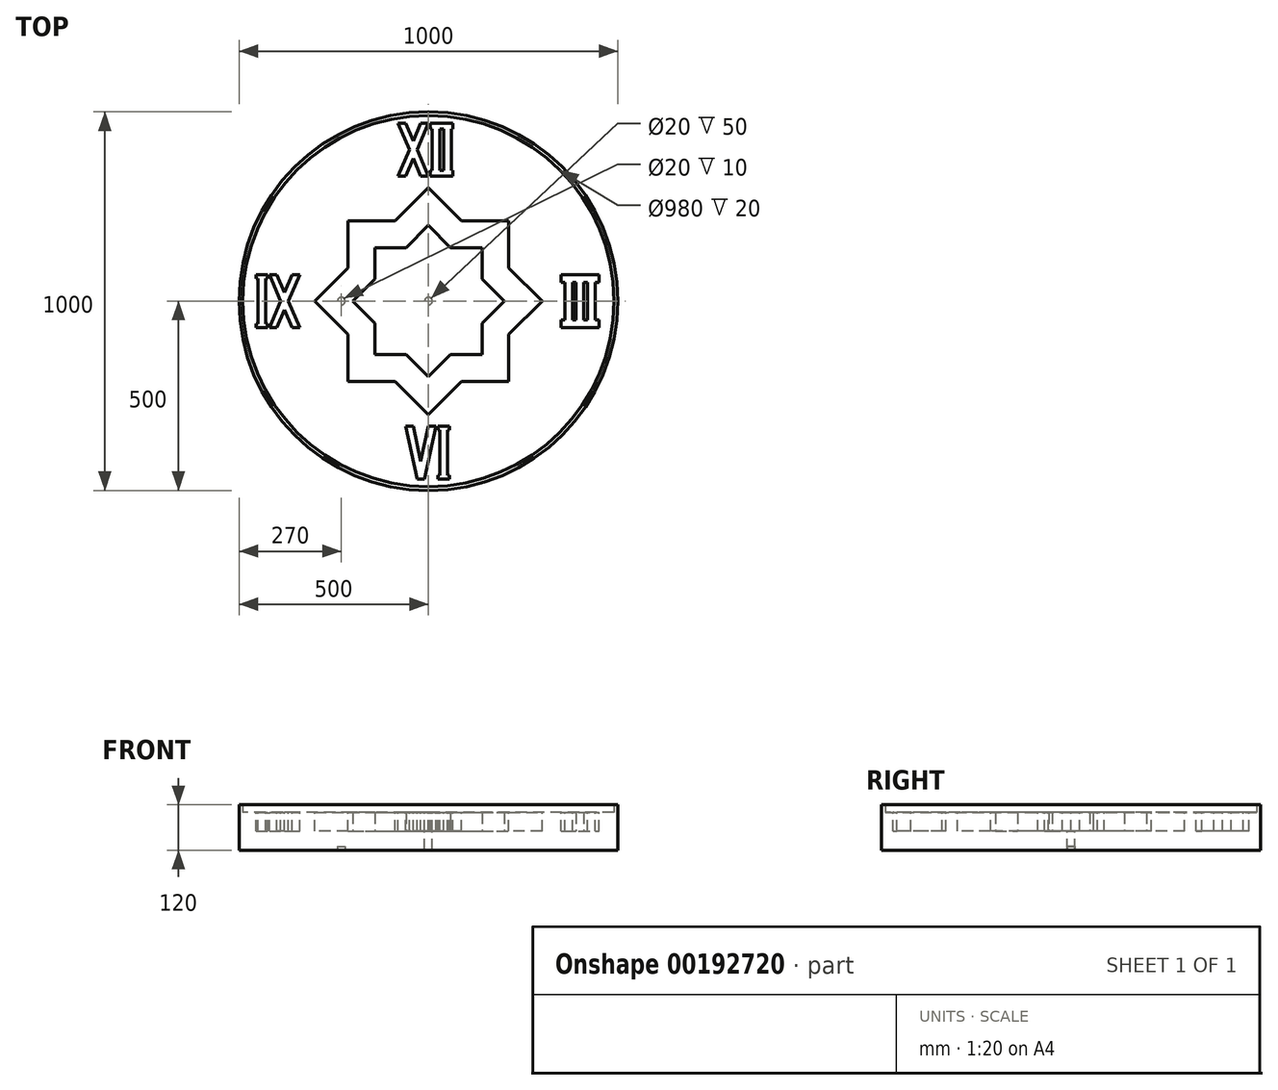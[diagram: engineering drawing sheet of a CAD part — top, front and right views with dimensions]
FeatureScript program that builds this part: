
annotation { "Feature Type Name" : "Feature", "Feature Type Description" : "" }
export const myFeature = defineFeature(function(context is Context, id is Id, definition is map)
    precondition{}
    {
        {
            var Q0;
            Q0=qCreatedBy(makeId("Top.planeOp"),FACE);
            var sketch = newSketch(context, id + "F0", { "sketchPlane" : qUnion([Q0])});
            skCircle(sketch, "E0", {"center": v(0, 0) * mm, "radius": 500 * mm});
            skSolve(sketch);
        }
        {
            var Q0;
            Q0 = qSketchRegion(id + "F0", true);
            extrude(context, id + "F1", {"entities" : qUnion([Q0]), "depth" : 100 * mm});
        }
        {
            var Q0;
            Q0=makeQuery(id+"F1.opExtrude","CAP_FACE",FACE,{"disambiguationData":[OSD([sQuery(id+"F0.wireOp",EDGE,"E0")])],"isStart":false});
            var sketch = newSketch(context, id + "F2", { "sketchPlane" : qUnion([Q0])});
            skCircle(sketch, "E1", {"center": v(0, 0) * mm, "radius": 10 * mm});
            skSolve(sketch);
        }
        {
            var Q0;
            Q0 = qSketchRegion(id + "F2", true);
            extrude(context, id + "F3", {"entities" : qUnion([Q0]), "operationType" : NewBodyOperationType.REMOVE, "endBound" : BoundingType.THROUGH_ALL, "oppositeDirection" : true, "depth" : 25 * mm});
        }
        {
            var Q0;
            Q0=makeQuery(id+"F1.opExtrude","CAP_FACE",FACE,{"disambiguationData":[OSD([sQuery(id+"F0.wireOp",EDGE,"E0")])],"isStart":false});
            var sketch = newSketch(context, id + "F4", { "sketchPlane" : qUnion([Q0])});
            skLineSegment(sketch, "E2", {"start": v(0, 0) * mm, "end": v(0, 400) * mm, "construction": true});
            skLineSegment(sketch, "E3", {"start": v(0, 400) * mm, "end": v(-40, 400) * mm, "construction": true});
            skLineSegment(sketch, "E4.bottom", {"start": v(-60, 470) * mm, "end": v(-20, 470) * mm, "construction": true});
            skLineSegment(sketch, "E4.top", {"start": v(-60, 330) * mm, "end": v(-20, 330) * mm, "construction": true});
            skLineSegment(sketch, "E4.left", {"start": v(-60, 470) * mm, "end": v(-60, 330) * mm, "construction": true});
            skLineSegment(sketch, "E4.right", {"start": v(-20, 470) * mm, "end": v(-20, 330) * mm, "construction": true});
            skPoint(sketch, "E4.middle", {"position": v(-40, 400) * mm});
            skLineSegment(sketch, "E5.bottom", {"start": v(-80, 470) * mm, "end": v(0, 470) * mm, "construction": true});
            skLineSegment(sketch, "E5.top", {"start": v(-80, 330) * mm, "end": v(0, 330) * mm, "construction": true});
            skLineSegment(sketch, "E5.left", {"start": v(-80, 470) * mm, "end": v(-80, 330) * mm, "construction": true});
            skLineSegment(sketch, "E5.right", {"start": v(0, 470) * mm, "end": v(0, 330) * mm, "construction": true});
            skLineSegment(sketch, "E6", {"start": v(-80, 470) * mm, "end": v(-20, 330) * mm});
            skLineSegment(sketch, "E7", {"start": v(-60, 470) * mm, "end": v(0, 330) * mm});
            skLineSegment(sketch, "E8", {"start": v(-20, 470) * mm, "end": v(-80, 330) * mm});
            skLineSegment(sketch, "E9", {"start": v(0, 470) * mm, "end": v(-60, 330) * mm});
            skLineSegment(sketch, "E10", {"start": v(-80, 470) * mm, "end": v(-60, 470) * mm});
            skLineSegment(sketch, "E11", {"start": v(-20, 470) * mm, "end": v(0, 470) * mm});
            skLineSegment(sketch, "E12", {"start": v(-80, 330) * mm, "end": v(-60, 330) * mm});
            skLineSegment(sketch, "E13", {"start": v(-20, 330) * mm, "end": v(0, 330) * mm});
            skLineSegment(sketch, "E14", {"start": v(0, 400) * mm, "end": v(20, 400) * mm, "construction": true});
            skLineSegment(sketch, "E15.bottom", {"start": v(10, 470) * mm, "end": v(30, 470) * mm});
            skLineSegment(sketch, "E15.top", {"start": v(10, 330) * mm, "end": v(30, 330) * mm});
            skLineSegment(sketch, "E15.left", {"start": v(10, 470) * mm, "end": v(10, 330) * mm});
            skLineSegment(sketch, "E15.right", {"start": v(30, 470) * mm, "end": v(30, 330) * mm});
            skPoint(sketch, "E15.middle", {"position": v(20, 400) * mm});
            skPoint(sketch, "E15.cornerSnap0", {"position": v(10, 400) * mm});
            skLineSegment(sketch, "E16", {"start": v(0, 400) * mm, "end": v(50, 400) * mm, "construction": true});
            skPoint(sketch, "E16.endSnap0", {"position": v(30, 400) * mm});
            skLineSegment(sketch, "E17.bottom", {"start": v(40, 470) * mm, "end": v(60, 470) * mm});
            skLineSegment(sketch, "E17.top", {"start": v(40, 330) * mm, "end": v(60, 330) * mm});
            skLineSegment(sketch, "E17.left", {"start": v(40, 470) * mm, "end": v(40, 330) * mm});
            skLineSegment(sketch, "E17.right", {"start": v(60, 470) * mm, "end": v(60, 330) * mm});
            skPoint(sketch, "E17.middle", {"position": v(50, 400) * mm});
            skLineSegment(sketch, "E18", {"start": v(10, 470) * mm, "end": v(5, 470) * mm, "construction": true});
            skLineSegment(sketch, "E19.bottom", {"start": v(5, 470) * mm, "end": v(65, 470) * mm});
            skLineSegment(sketch, "E19.top", {"start": v(5, 455) * mm, "end": v(65, 455) * mm});
            skLineSegment(sketch, "E19.left", {"start": v(5, 470) * mm, "end": v(5, 455) * mm});
            skLineSegment(sketch, "E19.right", {"start": v(65, 470) * mm, "end": v(65, 455) * mm});
            skLineSegment(sketch, "E20.MirrorCS", {"start": v(5, 330) * mm, "end": v(5, 345) * mm});
            skLineSegment(sketch, "E21.MirrorCS", {"start": v(5, 345) * mm, "end": v(65, 345) * mm});
            skLineSegment(sketch, "E22.MirrorCS", {"start": v(5, 330) * mm, "end": v(65, 330) * mm});
            skLineSegment(sketch, "E23.MirrorCS", {"start": v(65, 330) * mm, "end": v(65, 345) * mm});
            skSolve(sketch);
        }
        {
            var Q0;
            Q0 = qSketchRegion(id + "F4", true);
            extrude(context, id + "F5", {"entities" : qUnion([Q0]), "operationType" : NewBodyOperationType.REMOVE, "oppositeDirection" : true, "depth" : 50 * mm});
        }
        {
            var Q0;
            {var subQ19=sQuery(id+"F0.wireOp",EDGE,"E0");Q0=makeQuery(id+"F5.boolean.opBoolean","SPLIT",FACE,{"disambiguationData":[TD([makeQuery(id+"F1.opExtrude","SWEPT_FACE",FACE,{"disambiguationData":[OSD([subQ19])]})])],"derivedFrom":makeQuery(id+"F1.opExtrude","CAP_FACE",FACE,{"disambiguationData":[OSD([subQ19])],"isStart":false})});}
            var sketch = newSketch(context, id + "F6", { "sketchPlane" : qUnion([Q0])});
            skLineSegment(sketch, "E24", {"start": v(0, 0) * mm, "end": v(400, 0) * mm, "construction": true});
            skLineSegment(sketch, "E25.bottom", {"start": v(390, 70) * mm, "end": v(410, 70) * mm});
            skLineSegment(sketch, "E25.top", {"start": v(390, -70) * mm, "end": v(410, -70) * mm});
            skLineSegment(sketch, "E25.left", {"start": v(390, 70) * mm, "end": v(390, -70) * mm});
            skLineSegment(sketch, "E25.right", {"start": v(410, 70) * mm, "end": v(410, -70) * mm});
            skPoint(sketch, "E25.middle", {"position": v(400, 0) * mm});
            skLineSegment(sketch, "E26", {"start": v(400, 0) * mm, "end": v(370, 0) * mm, "construction": true});
            skLineSegment(sketch, "E27.bottom", {"start": v(360, 70) * mm, "end": v(380, 70) * mm});
            skLineSegment(sketch, "E27.top", {"start": v(360, -70) * mm, "end": v(380, -70) * mm});
            skLineSegment(sketch, "E27.left", {"start": v(360, 70) * mm, "end": v(360, -70) * mm});
            skLineSegment(sketch, "E27.right", {"start": v(380, 70) * mm, "end": v(380, -70) * mm});
            skPoint(sketch, "E27.middle", {"position": v(370, 0) * mm});
            skLineSegment(sketch, "E28", {"start": v(400, 0) * mm, "end": v(400, 173.06) * mm, "construction": true});
            skPoint(sketch, "E28.endSnap0", {"position": v(400, 70) * mm});
            skLineSegment(sketch, "E29.MirrorCS", {"start": v(420, 70) * mm, "end": v(420, -70) * mm});
            skLineSegment(sketch, "E30.MirrorCS", {"start": v(440, 70) * mm, "end": v(420, 70) * mm});
            skLineSegment(sketch, "E31.MirrorCS", {"start": v(440, 70) * mm, "end": v(440, -70) * mm});
            skLineSegment(sketch, "E32.MirrorCS", {"start": v(440, -70) * mm, "end": v(420, -70) * mm});
            skLineSegment(sketch, "E33", {"start": v(360, 70) * mm, "end": v(350, 70) * mm, "construction": true});
            skLineSegment(sketch, "E34.bottom", {"start": v(350, 70) * mm, "end": v(450, 70) * mm});
            skLineSegment(sketch, "E34.top", {"start": v(350, 50) * mm, "end": v(450, 50) * mm});
            skLineSegment(sketch, "E34.left", {"start": v(350, 70) * mm, "end": v(350, 50) * mm});
            skLineSegment(sketch, "E34.right", {"start": v(450, 70) * mm, "end": v(450, 50) * mm});
            skLineSegment(sketch, "E35.MirrorCS", {"start": v(350, -70) * mm, "end": v(350, -50) * mm});
            skLineSegment(sketch, "E36.MirrorCS", {"start": v(350, -50) * mm, "end": v(450, -50) * mm});
            skLineSegment(sketch, "E37.MirrorCS", {"start": v(350, -70) * mm, "end": v(450, -70) * mm});
            skLineSegment(sketch, "E38.MirrorCS", {"start": v(450, -70) * mm, "end": v(450, -50) * mm});
            skSolve(sketch);
        }
        {
            var Q0;
            Q0 = qSketchRegion(id + "F6", true);
            extrude(context, id + "F7", {"entities" : qUnion([Q0]), "operationType" : NewBodyOperationType.REMOVE, "oppositeDirection" : true, "depth" : 50 * mm});
        }
        {
            var Q0;
            {var subQ40=sQuery(id+"F0.wireOp",EDGE,"E0");var subQ41=makeQuery(id+"F1.opExtrude","SWEPT_FACE",FACE,{"disambiguationData":[OSD([subQ40])]});Q0=makeQuery(id+"F7.boolean.opBoolean","SPLIT",FACE,{"disambiguationData":[TD([subQ41])],"derivedFrom":makeQuery(id+"F5.boolean.opBoolean","SPLIT",FACE,{"disambiguationData":[TD([subQ41])],"derivedFrom":makeQuery(id+"F1.opExtrude","CAP_FACE",FACE,{"disambiguationData":[OSD([subQ40])],"isStart":false})})});}
            var sketch = newSketch(context, id + "F8", { "sketchPlane" : qUnion([Q0])});
            skLineSegment(sketch, "E39", {"start": v(0, 0) * mm, "end": v(400, 0) * mm, "construction": true});
            skPoint(sketch, "E39.endSnap0", {"position": v(360, 0) * mm});
            skLineSegment(sketch, "E40.bottom", {"start": v(390, 55) * mm, "end": v(410, 55) * mm});
            skLineSegment(sketch, "E40.top", {"start": v(390, -55) * mm, "end": v(410, -55) * mm});
            skLineSegment(sketch, "E40.left", {"start": v(390, 55) * mm, "end": v(390, -55) * mm});
            skLineSegment(sketch, "E40.right", {"start": v(410, 55) * mm, "end": v(410, -55) * mm});
            skPoint(sketch, "E40.middle", {"position": v(400, 0) * mm});
            skSolve(sketch);
        }
        {
            var Q0;
            Q0 = qSketchRegion(id + "F8", true);
            extrude(context, id + "F9", {"entities" : qUnion([Q0]), "operationType" : NewBodyOperationType.REMOVE, "oppositeDirection" : true, "depth" : 50 * mm});
        }
        {
            var Q0;
            {var subQ40=sQuery(id+"F0.wireOp",EDGE,"E0");var subQ41=makeQuery(id+"F1.opExtrude","SWEPT_FACE",FACE,{"disambiguationData":[OSD([subQ40])]});Q0=makeQuery(id+"F7.boolean.opBoolean","SPLIT",FACE,{"disambiguationData":[TD([subQ41])],"derivedFrom":makeQuery(id+"F5.boolean.opBoolean","SPLIT",FACE,{"disambiguationData":[TD([subQ41])],"derivedFrom":makeQuery(id+"F1.opExtrude","CAP_FACE",FACE,{"disambiguationData":[OSD([subQ40])],"isStart":false})})});}
            var sketch = newSketch(context, id + "F10", { "sketchPlane" : qUnion([Q0])});
            skLineSegment(sketch, "E41", {"start": v(0, 0) * mm, "end": v(0, -400) * mm, "construction": true});
            skLineSegment(sketch, "E42", {"start": v(0, -400) * mm, "end": v(-20, -400) * mm, "construction": true});
            skLineSegment(sketch, "E43.bottom", {"start": v(-40, -330) * mm, "end": v(0, -330) * mm, "construction": true});
            skLineSegment(sketch, "E43.top", {"start": v(-40, -470) * mm, "end": v(0, -470) * mm, "construction": true});
            skLineSegment(sketch, "E43.left", {"start": v(-40, -330) * mm, "end": v(-40, -470) * mm, "construction": true});
            skLineSegment(sketch, "E43.right", {"start": v(0, -330) * mm, "end": v(0, -470) * mm, "construction": true});
            skPoint(sketch, "E43.middle", {"position": v(-20, -400) * mm});
            skLineSegment(sketch, "E44.bottom", {"start": v(-60, -330) * mm, "end": v(20, -330) * mm, "construction": true});
            skLineSegment(sketch, "E44.top", {"start": v(-60, -470) * mm, "end": v(20, -470) * mm, "construction": true});
            skLineSegment(sketch, "E44.left", {"start": v(-60, -330) * mm, "end": v(-60, -470) * mm, "construction": true});
            skLineSegment(sketch, "E44.right", {"start": v(20, -330) * mm, "end": v(20, -470) * mm, "construction": true});
            skLineSegment(sketch, "E45.bottom", {"start": v(-30, -330) * mm, "end": v(-10, -330) * mm, "construction": true});
            skLineSegment(sketch, "E45.top", {"start": v(-30, -470) * mm, "end": v(-10, -470) * mm, "construction": true});
            skLineSegment(sketch, "E45.left", {"start": v(-30, -330) * mm, "end": v(-30, -470) * mm, "construction": true});
            skLineSegment(sketch, "E45.right", {"start": v(-10, -330) * mm, "end": v(-10, -470) * mm, "construction": true});
            skLineSegment(sketch, "E46", {"start": v(-60, -330) * mm, "end": v(-30, -470) * mm});
            skLineSegment(sketch, "E47", {"start": v(-40, -330) * mm, "end": v(-10, -470) * mm});
            skLineSegment(sketch, "E48", {"start": v(0, -330) * mm, "end": v(-30, -470) * mm});
            skLineSegment(sketch, "E49", {"start": v(20, -330) * mm, "end": v(-10, -470) * mm});
            skLineSegment(sketch, "E50", {"start": v(0, -330) * mm, "end": v(20, -330) * mm});
            skLineSegment(sketch, "E51", {"start": v(-40, -330) * mm, "end": v(-60, -330) * mm});
            skLineSegment(sketch, "E52", {"start": v(-30, -470) * mm, "end": v(-10, -470) * mm});
            skLineSegment(sketch, "E53", {"start": v(0, -400) * mm, "end": v(40, -400) * mm, "construction": true});
            skPoint(sketch, "E53.endSnap0", {"position": v(20, -400) * mm});
            skLineSegment(sketch, "E54.bottom", {"start": v(30, -330) * mm, "end": v(50, -330) * mm});
            skLineSegment(sketch, "E54.top", {"start": v(30, -470) * mm, "end": v(50, -470) * mm});
            skLineSegment(sketch, "E54.left", {"start": v(30, -330) * mm, "end": v(30, -470) * mm});
            skLineSegment(sketch, "E54.right", {"start": v(50, -330) * mm, "end": v(50, -470) * mm});
            skPoint(sketch, "E54.middle", {"position": v(40, -400) * mm});
            skLineSegment(sketch, "E55", {"start": v(30, -330) * mm, "end": v(25, -330) * mm, "construction": true});
            skLineSegment(sketch, "E56.bottom", {"start": v(25, -330) * mm, "end": v(55, -330) * mm});
            skLineSegment(sketch, "E56.top", {"start": v(25, -340) * mm, "end": v(55, -340) * mm});
            skLineSegment(sketch, "E56.left", {"start": v(25, -330) * mm, "end": v(25, -340) * mm});
            skLineSegment(sketch, "E56.right", {"start": v(55, -330) * mm, "end": v(55, -340) * mm});
            skLineSegment(sketch, "E57.MirrorCS", {"start": v(25, -470) * mm, "end": v(25, -460) * mm});
            skLineSegment(sketch, "E58.MirrorCS", {"start": v(25, -460) * mm, "end": v(55, -460) * mm});
            skLineSegment(sketch, "E59.MirrorCS", {"start": v(55, -470) * mm, "end": v(55, -460) * mm});
            skLineSegment(sketch, "E60.MirrorCS", {"start": v(25, -470) * mm, "end": v(55, -470) * mm});
            skSolve(sketch);
        }
        {
            var Q0;
            Q0 = qSketchRegion(id + "F10", true);
            extrude(context, id + "F11", {"entities" : qUnion([Q0]), "operationType" : NewBodyOperationType.REMOVE, "oppositeDirection" : true, "depth" : 50 * mm});
        }
        {
            var Q0;
            {var subQ40=sQuery(id+"F0.wireOp",EDGE,"E0");var subQ41=makeQuery(id+"F1.opExtrude","SWEPT_FACE",FACE,{"disambiguationData":[OSD([subQ40])]});Q0=makeQuery(id+"F7.boolean.opBoolean","SPLIT",FACE,{"disambiguationData":[TD([subQ41])],"derivedFrom":makeQuery(id+"F5.boolean.opBoolean","SPLIT",FACE,{"disambiguationData":[TD([subQ41])],"derivedFrom":makeQuery(id+"F1.opExtrude","CAP_FACE",FACE,{"disambiguationData":[OSD([subQ40])],"isStart":false})})});}
            var sketch = newSketch(context, id + "F12", { "sketchPlane" : qUnion([Q0])});
            skLineSegment(sketch, "E61", {"start": v(0, 0) * mm, "end": v(-400, 0) * mm, "construction": true});
            skLineSegment(sketch, "E62", {"start": v(-400, 0) * mm, "end": v(-380, 0) * mm, "construction": true});
            skLineSegment(sketch, "E63.bottom", {"start": v(-360, 70) * mm, "end": v(-400, 70) * mm, "construction": true});
            skLineSegment(sketch, "E63.top", {"start": v(-360, -70) * mm, "end": v(-400, -70) * mm, "construction": true});
            skLineSegment(sketch, "E63.left", {"start": v(-360, 70) * mm, "end": v(-360, -70) * mm, "construction": true});
            skLineSegment(sketch, "E63.right", {"start": v(-400, 70) * mm, "end": v(-400, -70) * mm, "construction": true});
            skPoint(sketch, "E63.middle", {"position": v(-380, 0) * mm});
            skLineSegment(sketch, "E64.bottom", {"start": v(-340, 70) * mm, "end": v(-420, 70) * mm, "construction": true});
            skLineSegment(sketch, "E64.top", {"start": v(-340, -70) * mm, "end": v(-420, -70) * mm, "construction": true});
            skLineSegment(sketch, "E64.left", {"start": v(-340, 70) * mm, "end": v(-340, -70) * mm, "construction": true});
            skLineSegment(sketch, "E64.right", {"start": v(-420, 70) * mm, "end": v(-420, -70) * mm, "construction": true});
            skLineSegment(sketch, "E65", {"start": v(-420, 70) * mm, "end": v(-360, -70) * mm});
            skLineSegment(sketch, "E66", {"start": v(-400, 70) * mm, "end": v(-340, -70) * mm});
            skLineSegment(sketch, "E67", {"start": v(-420, 70) * mm, "end": v(-400, 70) * mm});
            skLineSegment(sketch, "E68", {"start": v(-360, -70) * mm, "end": v(-340, -70) * mm});
            skLineSegment(sketch, "E69", {"start": v(-360, 70) * mm, "end": v(-340, 70) * mm});
            skLineSegment(sketch, "E70", {"start": v(-360, 70) * mm, "end": v(-420, -70) * mm});
            skLineSegment(sketch, "E71", {"start": v(-340, 70) * mm, "end": v(-400, -70) * mm});
            skLineSegment(sketch, "E72", {"start": v(-420, -70) * mm, "end": v(-400, -70) * mm});
            skLineSegment(sketch, "E73", {"start": v(-400, 0) * mm, "end": v(-440, 0) * mm, "construction": true});
            skLineSegment(sketch, "E74.bottom", {"start": v(-450, 70) * mm, "end": v(-430, 70) * mm});
            skLineSegment(sketch, "E74.top", {"start": v(-450, -70) * mm, "end": v(-430, -70) * mm});
            skLineSegment(sketch, "E74.left", {"start": v(-450, 70) * mm, "end": v(-450, -70) * mm});
            skLineSegment(sketch, "E74.right", {"start": v(-430, 70) * mm, "end": v(-430, -70) * mm});
            skPoint(sketch, "E74.middle", {"position": v(-440, 0) * mm});
            skLineSegment(sketch, "E75", {"start": v(-450, 70) * mm, "end": v(-455, 70) * mm, "construction": true});
            skLineSegment(sketch, "E76.bottom", {"start": v(-455, 70) * mm, "end": v(-425, 70) * mm});
            skLineSegment(sketch, "E76.top", {"start": v(-455, 60) * mm, "end": v(-425, 60) * mm});
            skLineSegment(sketch, "E76.left", {"start": v(-455, 70) * mm, "end": v(-455, 60) * mm});
            skLineSegment(sketch, "E76.right", {"start": v(-425, 70) * mm, "end": v(-425, 60) * mm});
            skLineSegment(sketch, "E77.MirrorCS", {"start": v(-455, -60) * mm, "end": v(-425, -60) * mm});
            skLineSegment(sketch, "E78.MirrorCS", {"start": v(-455, -70) * mm, "end": v(-455, -60) * mm});
            skLineSegment(sketch, "E79.MirrorCS", {"start": v(-425, -70) * mm, "end": v(-425, -60) * mm});
            skLineSegment(sketch, "E80.MirrorCS", {"start": v(-455, -70) * mm, "end": v(-425, -70) * mm});
            skSolve(sketch);
        }
        {
            var Q0;
            Q0 = qSketchRegion(id + "F12", true);
            extrude(context, id + "F13", {"entities" : qUnion([Q0]), "operationType" : NewBodyOperationType.REMOVE, "oppositeDirection" : true, "depth" : 50 * mm});
        }
        {
            var Q0;
            Q0=makeQuery(id+"F1.opExtrude","CAP_FACE",FACE,{"disambiguationData":[OSD([sQuery(id+"F0.wireOp",EDGE,"E0")])],"isStart":true});
            var sketch = newSketch(context, id + "F14", { "sketchPlane" : qUnion([Q0])});
            skLineSegment(sketch, "E81", {"start": v(0, 0) * mm, "end": v(-230, 0) * mm, "construction": true});
            skCircle(sketch, "E82", {"center": v(-230, 0) * mm, "radius": 10 * mm});
            skSolve(sketch);
        }
        {
            var Q0;
            Q0 = qSketchRegion(id + "F14", true);
            extrude(context, id + "F15", {"entities" : qUnion([Q0]), "operationType" : NewBodyOperationType.REMOVE, "oppositeDirection" : true, "depth" : 10 * mm});
        }
        {
            var Q0;
            {var subQ40=sQuery(id+"F0.wireOp",EDGE,"E0");var subQ41=makeQuery(id+"F1.opExtrude","SWEPT_FACE",FACE,{"disambiguationData":[OSD([subQ40])]});Q0=makeQuery(id+"F7.boolean.opBoolean","SPLIT",FACE,{"disambiguationData":[TD([subQ41])],"derivedFrom":makeQuery(id+"F5.boolean.opBoolean","SPLIT",FACE,{"disambiguationData":[TD([subQ41])],"derivedFrom":makeQuery(id+"F1.opExtrude","CAP_FACE",FACE,{"disambiguationData":[OSD([subQ40])],"isStart":false})})});}
            var sketch = newSketch(context, id + "F16", { "sketchPlane" : qUnion([Q0])});
            skCircle(sketch, "E83", {"center": v(0, 0) * mm, "radius": 500 * mm});
            skCircle(sketch, "E84", {"center": v(0, 0) * mm, "radius": 490 * mm});
            skSolve(sketch);
        }
        {
            var Q0;
            Q0 = qSketchRegion(id + "F16", true);
            extrude(context, id + "F17", {"entities" : qUnion([Q0]), "operationType" : NewBodyOperationType.ADD, "depth" : 20 * mm});
        }
        {
            var Q0;
            {var subQ40=sQuery(id+"F0.wireOp",EDGE,"E0");var subQ41=makeQuery(id+"F1.opExtrude","SWEPT_FACE",FACE,{"disambiguationData":[OSD([subQ40])]});Q0=makeQuery(id+"F7.boolean.opBoolean","SPLIT",FACE,{"disambiguationData":[TD([subQ41])],"derivedFrom":makeQuery(id+"F5.boolean.opBoolean","SPLIT",FACE,{"disambiguationData":[TD([subQ41])],"derivedFrom":makeQuery(id+"F1.opExtrude","CAP_FACE",FACE,{"disambiguationData":[OSD([subQ40])],"isStart":false})})});}
            var sketch = newSketch(context, id + "F18", { "sketchPlane" : qUnion([Q0])});
            skLineSegment(sketch, "E85", {"start": v(0, 0) * mm, "end": v(300, 0) * mm, "construction": true});
            skPoint(sketch, "E85.endSnap0", {"position": v(360, 0) * mm});
            skLineSegment(sketch, "E86", {"start": v(0, 0) * mm, "end": v(0, 300) * mm, "construction": true});
            skLineSegment(sketch, "E87.MirrorCS", {"start": v(0, 0) * mm, "end": v(0, -300) * mm, "construction": true});
            skLineSegment(sketch, "E88.MirrorCS", {"start": v(0, 0) * mm, "end": v(-300, 0) * mm, "construction": true});
            skLineSegment(sketch, "E89", {"start": v(0, 300) * mm, "end": v(-300, 0) * mm});
            skLineSegment(sketch, "E90", {"start": v(-300, 0) * mm, "end": v(0, -300) * mm});
            skLineSegment(sketch, "E91", {"start": v(300, 0) * mm, "end": v(0, -300) * mm});
            skLineSegment(sketch, "E92", {"start": v(0, 300) * mm, "end": v(300, 0) * mm});
            skLineSegment(sketch, "E93.bottom", {"start": v(-212.13, 212.13) * mm, "end": v(212.13, 212.13) * mm});
            skLineSegment(sketch, "E93.top", {"start": v(-212.13, -212.13) * mm, "end": v(212.13, -212.13) * mm});
            skLineSegment(sketch, "E93.left", {"start": v(-212.13, 212.13) * mm, "end": v(-212.13, -212.13) * mm});
            skLineSegment(sketch, "E93.right", {"start": v(212.13, 212.13) * mm, "end": v(212.13, -212.13) * mm});
            skPoint(sketch, "E93.middle", {"position": v(0, 0) * mm});
            skSolve(sketch);
        }
        {
            var Q0;
            Q0 = qSketchRegion(id + "F18", true);
            extrude(context, id + "F19", {"entities" : qUnion([Q0]), "operationType" : NewBodyOperationType.REMOVE, "oppositeDirection" : true, "depth" : 50 * mm});
        }
        {
            var Q0;
            Q0=makeQuery(id+"F19.boolean.opBoolean","COPY",FACE,{"derivedFrom":makeQuery(id+"F19.opExtrude","CAP_FACE",FACE,{"disambiguationData":[OSD([sQuery(id+"F18.wireOp",EDGE,"E89"),sQuery(id+"F18.wireOp",EDGE,"E90"),sQuery(id+"F18.wireOp",EDGE,"E91"),sQuery(id+"F18.wireOp",EDGE,"E92"),sQuery(id+"F18.wireOp",EDGE,"E93.bottom"),sQuery(id+"F18.wireOp",EDGE,"E93.top"),sQuery(id+"F18.wireOp",EDGE,"E93.left"),sQuery(id+"F18.wireOp",EDGE,"E93.right")])],"isStart":false})});
            var sketch = newSketch(context, id + "F20", { "sketchPlane" : qUnion([Q0])});
            skLineSegment(sketch, "E94", {"start": v(0, 0) * mm, "end": v(0, 200) * mm, "construction": true});
            skLineSegment(sketch, "E95", {"start": v(0, 0) * mm, "end": v(200, 0) * mm, "construction": true});
            skLineSegment(sketch, "E96.MirrorCS", {"start": v(0, 0) * mm, "end": v(0, -200) * mm, "construction": true});
            skLineSegment(sketch, "E97.MirrorCS", {"start": v(0, 0) * mm, "end": v(-200, 0) * mm, "construction": true});
            skLineSegment(sketch, "E98", {"start": v(0, 200) * mm, "end": v(-200, 0) * mm});
            skLineSegment(sketch, "E99", {"start": v(-200, 0) * mm, "end": v(0, -200) * mm});
            skLineSegment(sketch, "E100", {"start": v(0, 200) * mm, "end": v(200, 0) * mm});
            skLineSegment(sketch, "E101", {"start": v(0, -200) * mm, "end": v(200, 0) * mm});
            skLineSegment(sketch, "E102.bottom", {"start": v(-141.42, 141.42) * mm, "end": v(141.42, 141.42) * mm});
            skLineSegment(sketch, "E102.top", {"start": v(-141.42, -141.42) * mm, "end": v(141.42, -141.42) * mm});
            skLineSegment(sketch, "E102.left", {"start": v(-141.42, 141.42) * mm, "end": v(-141.42, -141.42) * mm});
            skLineSegment(sketch, "E102.right", {"start": v(141.42, 141.42) * mm, "end": v(141.42, -141.42) * mm});
            skPoint(sketch, "E102.middle", {"position": v(0, 0) * mm});
            skSolve(sketch);
        }
        {
            var Q0;
            Q0 = qSketchRegion(id + "F20", true);
            extrude(context, id + "F21", {"entities" : qUnion([Q0]), "operationType" : NewBodyOperationType.ADD, "depth" : 50 * mm});
        }
    });
